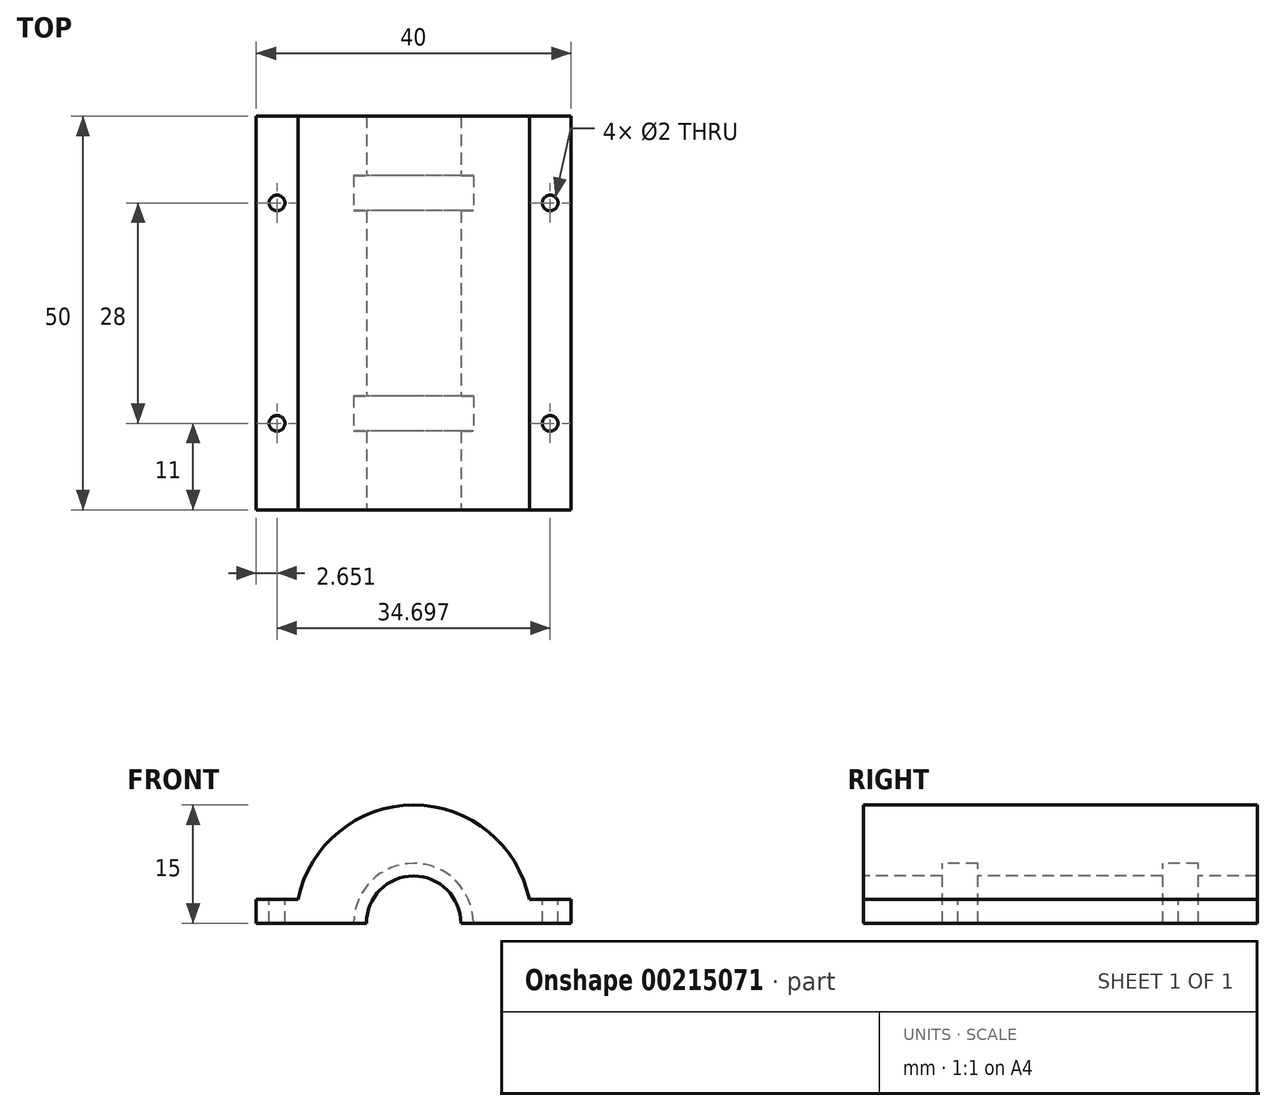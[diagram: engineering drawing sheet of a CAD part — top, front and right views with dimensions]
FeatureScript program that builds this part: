
annotation { "Feature Type Name" : "Feature", "Feature Type Description" : "" }
export const myFeature = defineFeature(function(context is Context, id is Id, definition is map)
    precondition{}
    {
        {
            var Q0;
            Q0=qCreatedBy(makeId("Front.planeOp"),FACE);
            var sketch = newSketch(context, id + "F0", { "sketchPlane" : qUnion([Q0])});
            skLineSegment(sketch, "E0", {"start": v(0, 0) * mm, "end": v(14, 0) * mm});
            skArc(sketch, "E1.0", {"start": v(35, 0) * mm, "mid": v(20, 15) * mm, "end": v(5, 0) * mm});
            skLineSegment(sketch, "E2", {"start": v(5, 0) * mm, "end": v(0, 0) * mm});
            skLineSegment(sketch, "E3", {"start": v(0, 0) * mm, "end": v(0, 3) * mm});
            skLineSegment(sketch, "E4", {"start": v(0, 3) * mm, "end": v(5.3, 3) * mm});
            skLineSegment(sketch, "E5", {"start": v(20, 15) * mm, "end": v(20, 6) * mm, "construction": true});
            skLineSegment(sketch, "E6.MirrorCS", {"start": v(40, 3) * mm, "end": v(34.7, 3) * mm});
            skLineSegment(sketch, "E7.MirrorCS", {"start": v(40, 0) * mm, "end": v(40, 3) * mm});
            skArc(sketch, "E8", {"start": v(26, 0) * mm, "mid": v(20, 6) * mm, "end": v(14, 0) * mm});
            skLineSegment(sketch, "E9.trimOffspring", {"start": v(26, 0) * mm, "end": v(40, 0) * mm});
            skSolve(sketch);
        }
        {
            var Q0;
            Q0 = qSketchRegion(id + "F0", true);
            extrude(context, id + "F1", {"entities" : qUnion([Q0]), "oppositeDirection" : true, "depth" : 50 * mm});
        }
        {
            var Q0;
            Q0=makeQuery(id+"F1.opExtrude","CAP_FACE",FACE,{"disambiguationData":[OSD([sQuery(id+"F0.wireOp",EDGE,"E0"),sQuery(id+"F0.wireOp",EDGE,"E1.0"),sQuery(id+"F0.wireOp",EDGE,"E2"),sQuery(id+"F0.wireOp",EDGE,"E3"),sQuery(id+"F0.wireOp",EDGE,"E4"),sQuery(id+"F0.wireOp",EDGE,"E6.MirrorCS"),sQuery(id+"F0.wireOp",EDGE,"E7.MirrorCS"),sQuery(id+"F0.wireOp",EDGE,"E8"),sQuery(id+"F0.wireOp",EDGE,"E9.trimOffspring")])],"isStart":true});
            cPlane(context, id + "F2", {"entities" : qUnion([Q0]), "cplaneType" : CPlaneType.OFFSET, "offset" : 10 * mm, "oppositeDirection" : true, "width" : 150 * mm, "height" : 150 * mm});
        }
        {
            var Q0;
            Q0=qCreatedBy(id+"F2.planeOp",FACE);
            var sketch = newSketch(context, id + "F3", { "sketchPlane" : qUnion([Q0])});
            skLineSegment(sketch, "E10", {"start": v(0, 0) * mm, "end": v(40, 0) * mm, "construction": true});
            skLineSegment(sketch, "E11", {"start": v(20, 0) * mm, "end": v(20, 19.68) * mm, "construction": true});
            skArc(sketch, "E12", {"start": v(27.6, 0) * mm, "mid": v(20, 7.6) * mm, "end": v(12.4, 0) * mm});
            skArc(sketch, "E13", {"start": v(26, 0) * mm, "mid": v(20, 6) * mm, "end": v(14, 0) * mm});
            skLineSegment(sketch, "E14", {"start": v(12.4, 0) * mm, "end": v(14, 0) * mm});
            skLineSegment(sketch, "E15", {"start": v(26, 0) * mm, "end": v(27.6, 0) * mm});
            skSolve(sketch);
        }
        {
            var Q0;
            Q0 = qSketchRegion(id + "F3", true);
            extrude(context, id + "F4", {"entities" : qUnion([Q0]), "operationType" : NewBodyOperationType.REMOVE, "oppositeDirection" : true, "depth" : 4.5 * mm});
        }
        {
            var Q0;
            Q0 = qSketchRegion(id + "F3", true);
            extrude(context, id + "F5", {"entities" : qUnion([Q0]), "operationType" : NewBodyOperationType.REMOVE, "oppositeDirection" : true, "depth" : 32.5 * mm, "hasSecondDirection" : true, "secondDirectionOppositeDirection" : true, "secondDirectionDepth" : 28 * mm});
        }
        {
            var Q0;
            Q0=makeQuery(id+"F1.opExtrude","SWEPT_FACE",FACE,{"disambiguationData":[OSD([sQuery(id+"F0.wireOp",EDGE,"E6.MirrorCS")])]});
            var sketch = newSketch(context, id + "F6", { "sketchPlane" : qUnion([Q0])});
            skLineSegment(sketch, "E16", {"start": v(37.35, 0) * mm, "end": v(37.35, 50) * mm, "construction": true});
            skCircle(sketch, "E17", {"center": v(37.35, 11) * mm, "radius": 1 * mm});
            skCircle(sketch, "E18", {"center": v(37.35, 39) * mm, "radius": 1 * mm});
            skLineSegment(sketch, "E19", {"start": v(0, 0) * mm, "end": v(40, 0) * mm, "construction": true});
            skLineSegment(sketch, "E20", {"start": v(20, 0) * mm, "end": v(20, 51.2) * mm, "construction": true});
            skCircle(sketch, "E21.MirrorC", {"center": v(2.65, 11) * mm, "radius": 1 * mm});
            skCircle(sketch, "E22.MirrorC", {"center": v(2.65, 39) * mm, "radius": 1 * mm});
            skSolve(sketch);
        }
        {
            var Q0;
            Q0 = qSketchRegion(id + "F6", true);
            extrude(context, id + "F7", {"entities" : qUnion([Q0]), "operationType" : NewBodyOperationType.REMOVE, "oppositeDirection" : true, "depth" : 25 * mm});
        }
    });
